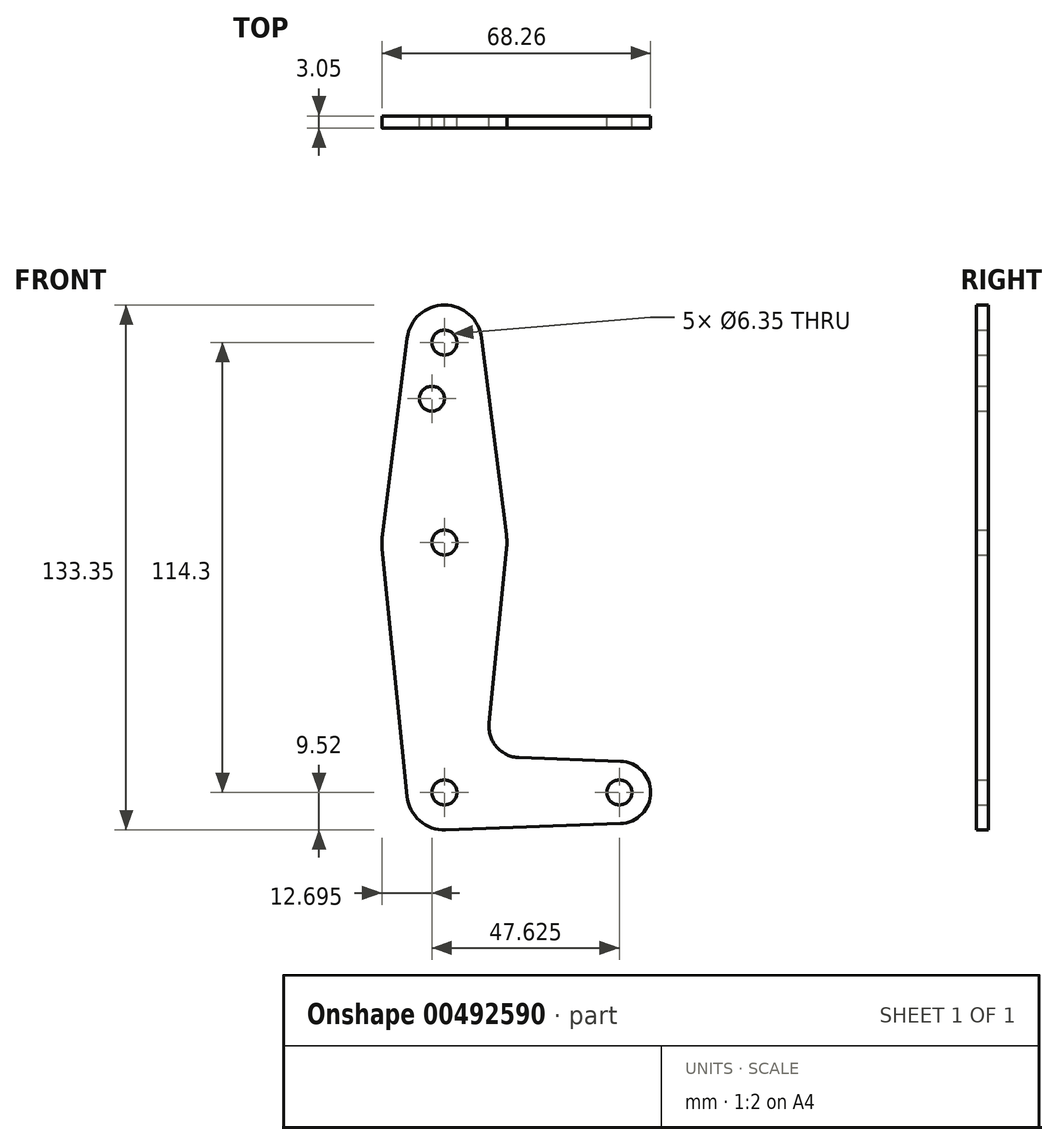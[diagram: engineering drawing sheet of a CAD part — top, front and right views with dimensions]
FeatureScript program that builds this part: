
annotation { "Feature Type Name" : "Feature", "Feature Type Description" : "" }
export const myFeature = defineFeature(function(context is Context, id is Id, definition is map)
    precondition{}
    {
        {
            var Q0;
            Q0=qCreatedBy(makeId("Front.planeOp"),FACE);
            var sketch = newSketch(context, id + "F0", { "sketchPlane" : qUnion([Q0])});
            skLineSegment(sketch, "E0", {"start": v(0, 0) * mm, "end": v(0, 9.52) * mm, "construction": true});
            skLineSegment(sketch, "E1", {"start": v(0, 0) * mm, "end": v(44.45, 0) * mm, "construction": true});
            skCircle(sketch, "E2", {"center": v(0, 0) * mm, "radius": 9.53 * mm});
            skCircle(sketch, "E3", {"center": v(44.45, 0) * mm, "radius": 7.94 * mm});
            skCircle(sketch, "E4", {"center": v(0, 114.3) * mm, "radius": 9.53 * mm});
            skCircle(sketch, "E5", {"center": v(0, 63.5) * mm, "radius": 15.88 * mm});
            skLineSegment(sketch, "E6", {"start": v(0, 63.5) * mm, "end": v(0, 47.62) * mm});
            skLineSegment(sketch, "E7.trimOffspring", {"start": v(0, 47.62) * mm, "end": v(0, 114.3) * mm, "construction": true});
            skLineSegment(sketch, "E8.trimOffspring", {"start": v(0, 9.53) * mm, "end": v(0, 0) * mm});
            skLineSegment(sketch, "E9", {"start": v(0, 63.5) * mm, "end": v(0, 9.52) * mm, "construction": true});
            skLineSegment(sketch, "E10", {"start": v(9.45, 115.5) * mm, "end": v(15.75, 65.48) * mm});
            skLineSegment(sketch, "E11", {"start": v(-9.45, 115.5) * mm, "end": v(-15.75, 65.48) * mm});
            skLineSegment(sketch, "E12", {"start": v(44.73, -7.93) * mm, "end": v(0.34, -9.52) * mm});
            skLineSegment(sketch, "E13", {"start": v(44.73, 7.93) * mm, "end": v(18.97, 8.85) * mm});
            skLineSegment(sketch, "E14", {"start": v(15.8, 61.91) * mm, "end": v(11.34, 17.6) * mm});
            skLineSegment(sketch, "E15", {"start": v(-15.8, 61.91) * mm, "end": v(-9.48, -0.95) * mm});
            skCircle(sketch, "E16", {"center": v(0, 114.3) * mm, "radius": 3.18 * mm});
            skCircle(sketch, "E17", {"center": v(-3.18, 100.03) * mm, "radius": 3.18 * mm});
            skCircle(sketch, "E18", {"center": v(0, 63.5) * mm, "radius": 3.18 * mm});
            skCircle(sketch, "E19", {"center": v(0, 0) * mm, "radius": 3.18 * mm});
            skCircle(sketch, "E20", {"center": v(44.45, 0) * mm, "radius": 3.18 * mm});
            skArc(sketch, "E21.filletArc", {"start": v(11.34, 17.6) * mm, "mid": v(13.26, 11.57) * mm, "end": v(18.97, 8.85) * mm});
            skSolve(sketch);
        }
        {
            var Q0;
            Q0 = qSketchRegion(id + "F0", true);
            extrude(context, id + "F1", {"entities" : qUnion([Q0]), "depth" : 3.05 * mm});
        }
    });
